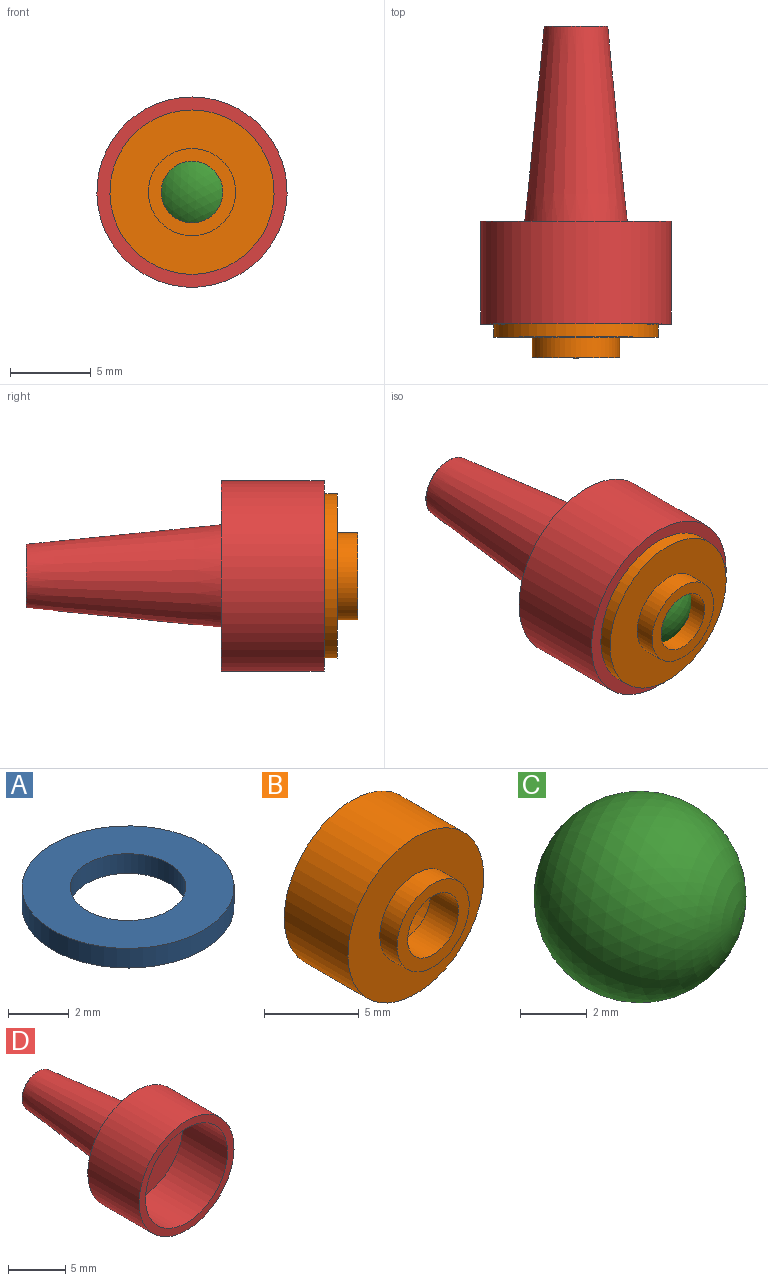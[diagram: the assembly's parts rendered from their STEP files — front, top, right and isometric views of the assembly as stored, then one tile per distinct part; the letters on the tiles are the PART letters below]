
ASSEMBLY  parts=4 mates=6
PART A: 4 faces, bbox 7x7x0.8 mm
  f0: cylinder r=1.91mm len=3.81mm, axis (0,0,-1), area 9.5mm2, adj f2,f3
  f1: cylinder r=3.49mm len=6.99mm, axis (0,0,-1), area 17.4mm2, adj f2,f3
  f2: plane 6.99x6.99mm, normal (0,0,1), area 26.9mm2, adj f0,f1
  f3: plane 6.99x6.99mm, normal (0,0,-1), area 26.9mm2, adj f0,f1
PART B: 8 faces, bbox 10.2x6.1x10.2 mm
  f0: cylinder r=4.27mm len=8.55mm, axis (0,1,0), area 106.2mm2, adj f1,f7
  f1: plane 10.16x10.16mm, normal (0,1,0), area 23.7mm2, adj f0,f2
  f2: cylinder r=5.08mm len=10.16mm, axis (0,1,0), area 152mm2, adj f1,f3
  f3: plane 10.16x10.16mm, normal (0,-1,0), area 58.2mm2, adj f2,f4
  f4: cylinder r=2.7mm len=5.4mm, axis (0,1,0), area 21.9mm2, adj f3,f5
  f5: plane 5.4x5.4mm, normal (0,-1,0), area 11.5mm2, adj f4,f6
  f6: cylinder r=1.91mm len=3.81mm, axis (0,1,0), area 25.1mm2, adj f5,f7
  f7: plane 8.55x8.55mm, normal (0,1,0), area 46mm2, adj f0,f6
PART C: 1 faces, bbox 6.4x6.4x6.4 mm
  f0: sphere r=3.17mm, area 126.7mm2
PART D: 8 faces, bbox 11.8x18.4x11.8 mm
  f0: cylinder r=5.89mm len=11.77mm, axis (0,1,0), area 234.9mm2, adj f1,f7
  f1: plane 11.77x11.77mm, normal (0,-1,0), area 27.8mm2, adj f0,f2
  f2: cylinder r=5.08mm len=10.16mm, axis (0,1,0), area 177mm2, adj f1,f3
  f3: plane 10.16x10.16mm, normal (0,-1,0), area 69.7mm2, adj f2,f4
  f4: cylinder r=1.91mm len=12.87mm, axis (0,1,0), area 154.1mm2, adj f3,f5
  f5: torus R=1.94mm, axis (0,1,0), area 1.2mm2, adj f4,f6
  f6: cone r=1.97mm half-angle=5.7deg, axis (0,-1,0), area 196mm2, adj f5,f7
  f7: plane 11.77x11.77mm, normal (0,1,0), area 77.2mm2, adj f0,f6
PLACE A rot(axis=(-1,0,0),90deg) t=(2.54,-3.15,-10.71)mm
PLACE B t=(15.62,42.71,41.11)mm
PLACE C rot(axis=(1,0,0),90deg) t=(7.43,-6.33,99.16)mm
PLACE D t=(15.62,42.73,41.11)mm
MATE cylindrical B.f0 <-> C.f0  axis (0,1,0) through (-32.72,-10,41.11)mm
MATE planar A.f0 <-> D.f0  axis (0,1,0) through (-32.72,-2.36,41.11)mm
MATE planar B.f0 <-> D.f0  axis (0,1,0) through (-32.72,-7.9,41.11)mm
MATE fastened C.f0 <-> A.f0  axis (0,-1,0) through (-32.72,-6.33,41.11)mm
MATE cylindrical B.f0 <-> D.f0  axis (0,1,0) through (-32.72,-3.94,41.11)mm
MATE cylindrical A.f0 <-> D.f0  axis (0,-1,0) through (-32.72,-3.15,41.11)mm
